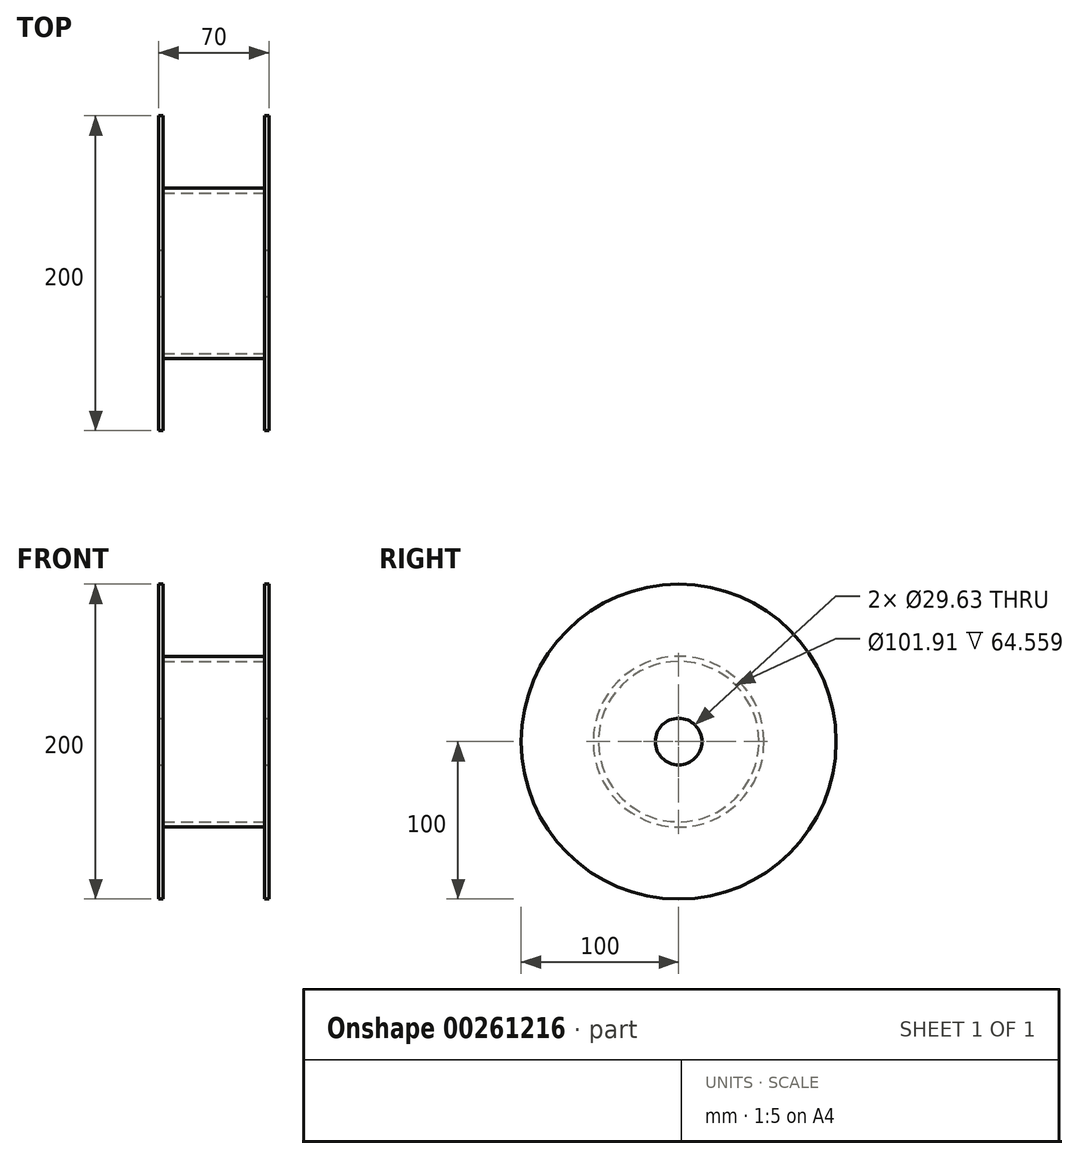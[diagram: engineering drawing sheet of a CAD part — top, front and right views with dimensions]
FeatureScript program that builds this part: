
annotation { "Feature Type Name" : "Feature", "Feature Type Description" : "" }
export const myFeature = defineFeature(function(context is Context, id is Id, definition is map)
    precondition{}
    {
        {
            var Q0;
            Q0=qCreatedBy(makeId("Front.planeOp"),FACE);
            var sketch = newSketch(context, id + "F0", { "sketchPlane" : qUnion([Q0])});
            skLineSegment(sketch, "E0.top", {"start": v(-54.4, -150.38) * mm, "end": v(-51.75, -150.38) * mm});
            skLineSegment(sketch, "E1", {"start": v(15.6, -50.38) * mm, "end": v(-54.4, -50.38) * mm});
            skLineSegment(sketch, "E2.top", {"start": v(-51.75, -101.34) * mm, "end": v(12.81, -101.34) * mm});
            skLineSegment(sketch, "E2.left", {"start": v(-51.75, -65.2) * mm, "end": v(-51.75, -101.34) * mm});
            skLineSegment(sketch, "E2.right", {"start": v(12.81, -65.2) * mm, "end": v(12.81, -101.34) * mm});
            skLineSegment(sketch, "E3", {"start": v(-54.4, -65.2) * mm, "end": v(-51.75, -65.2) * mm});
            skLineSegment(sketch, "E4.trimOffspring", {"start": v(15.6, -65.2) * mm, "end": v(15.6, -150.38) * mm});
            skLineSegment(sketch, "E5.trimOffspring", {"start": v(12.81, -65.2) * mm, "end": v(15.6, -65.2) * mm});
            skLineSegment(sketch, "E6.trimOffspring", {"start": v(-54.4, -65.2) * mm, "end": v(-54.4, -150.38) * mm});
            skPoint(sketch, "E0.bottom.end.orphan", {"position": v(15.6, 49.62) * mm});
            skPoint(sketch, "E0.bottom.start.orphan", {"position": v(-54.4, 49.62) * mm});
            skLineSegment(sketch, "E7.bottom", {"start": v(-51.75, -104.65) * mm, "end": v(12.81, -104.65) * mm});
            skLineSegment(sketch, "E7.left", {"start": v(-51.75, -104.65) * mm, "end": v(-51.75, -150.38) * mm});
            skLineSegment(sketch, "E7.right", {"start": v(12.81, -104.65) * mm, "end": v(12.81, -150.38) * mm});
            skLineSegment(sketch, "E8.trimOffspring", {"start": v(12.81, -150.38) * mm, "end": v(15.6, -150.38) * mm});
            skSolve(sketch);
        }
        {
            var Q0;
            Q0=qSketchRegion(id+"F0",true);
            var Q1;
            Q1=sQuery(id+"F0.wireOp",EDGE,"E1");
            revolve(context, id + "F1", {"entities" : qUnion([Q0]), "axis" : qUnion([Q1]), "revolveType" : RevolveType.FULL});
        }
    });
